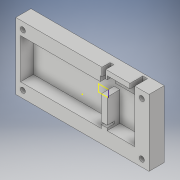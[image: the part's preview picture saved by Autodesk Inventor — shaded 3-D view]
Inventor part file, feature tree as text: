
AUTODESK INVENTOR PART (.ipt)
format: ipt  version: 2018 (Build 220112000, 112)  size: 253,952 bytes
history: native  units: in
note: dims shown in document units (in); Inventor stores cm internally (conversion verified against a paired STEP export)
features: extrude x10, sketch x7, plane x4, projected_geometry x4, hole x2
ambient origin geometry x8: Origin, YZ Plane, XZ Plane, XY Plane, X Axis, Y Axis, Z Axis, Center Point
bodies: Solid1 (feature_tree)
feature tree (27):
  extrude  "Extrusion1"  Depth=3.5in
  extrude  "Extrusion2"  Depth=2.105in
  extrude  "Extrusion4"  Depth=0.25in
  plane  "Work Plane1"
  plane  "Work Plane2"
  extrude  "Extrusion5"  Depth=0.38in
  plane  "Work Plane3"
  plane  "Work Plane4"
  sketch  "Sketch6"  dims[d4=0.25in d5=4.075in]
  extrude  "Extrusion6"  Depth=0.675in
  extrude  "Extrusion7"  Depth=0.2in
  extrude  "Extrusion8"  Depth=0.125in TaperAngle=0.0deg
  extrude  "Extrusion9"  Depth=0.0625in
  extrude  "Extrusion10"  Depth=1.0in
  extrude  "Extrusion11"  Depth=1.45in
  hole  "Hole3"  [1 undecoded]
  sketch  "Sketch3"  dims[d0=7.0in d1=3.5in]
  projected_geometry  "Projected Loop2"
  sketch  "Sketch5"  dims[d2=4.25in d3=2.105in]
  projected_geometry  "Projected Loop3"
  sketch  "Sketch7"  dims[d7=0.33in d8=0.38in]
  projected_geometry  "Projected Loop4"
  sketch  "Sketch8"  dims[d9=0.675in d10=0.0in d13=0.525in]
  sketch  "Sketch10"  dims[d15=0.2in d17=0.4in]
  projected_geometry  "Projected Loop5"
  sketch  "Sketch11"  dims[d18=0.5in d19=0.0in d22=0.125in d23=0.0in d24=0.0625in d25=0.22in d26=1.45in d27=2.0in d28=0.75in d29=0.25in d30=0.125in d31=0.0in d32=0.5in d33=0.125in d34=0.125in d35=0.875in d36=0.375in d37=0.0in d38=0.375in d39=0.0in d40=0.25in d41=0.0in d42=0.25in d43=0.0in d44=0.25in d45=0.0in d53=0.25in d54=0.0in d55=0.266in d56=0.75in d57=0.375in d58=0.25in d59=0.5635in d60=1.0in d61=0.0in]
  hole  "Hole2"  [1 undecoded]
note: 2 required parameter values undecoded (feature->parameter linkage not recoverable at this tier; creation-order binding heuristic only, values carry confidence <= 0.55)
